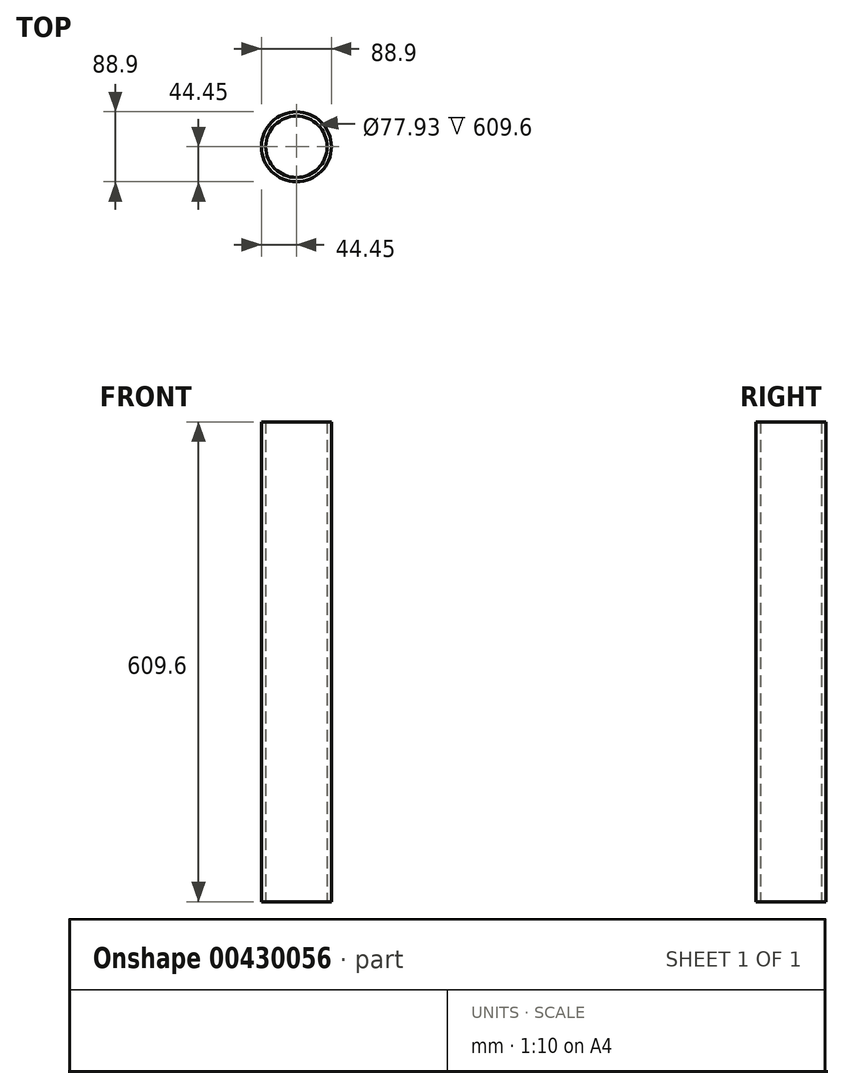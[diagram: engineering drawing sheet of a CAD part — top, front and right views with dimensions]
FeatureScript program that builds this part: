
annotation { "Feature Type Name" : "Feature", "Feature Type Description" : "" }
export const myFeature = defineFeature(function(context is Context, id is Id, definition is map)
    precondition{}
    {
        {
            var Q0;
            Q0=qCreatedBy(makeId("Top.planeOp"),FACE);
            var sketch = newSketch(context, id + "F0", { "sketchPlane" : qUnion([Q0])});
            skCircle(sketch, "E0", {"center": v(0, 0) * mm, "radius": 44.45 * mm});
            skCircle(sketch, "E1", {"center": v(0, 0) * mm, "radius": 38.96 * mm});
            skSolve(sketch);
        }
        {
            var Q0;
            Q0 = qSketchRegion(id + "F0", true);
            extrude(context, id + "F1", {"entities" : qUnion([Q0]), "depth" : 609.6 * mm});
        }
    });
